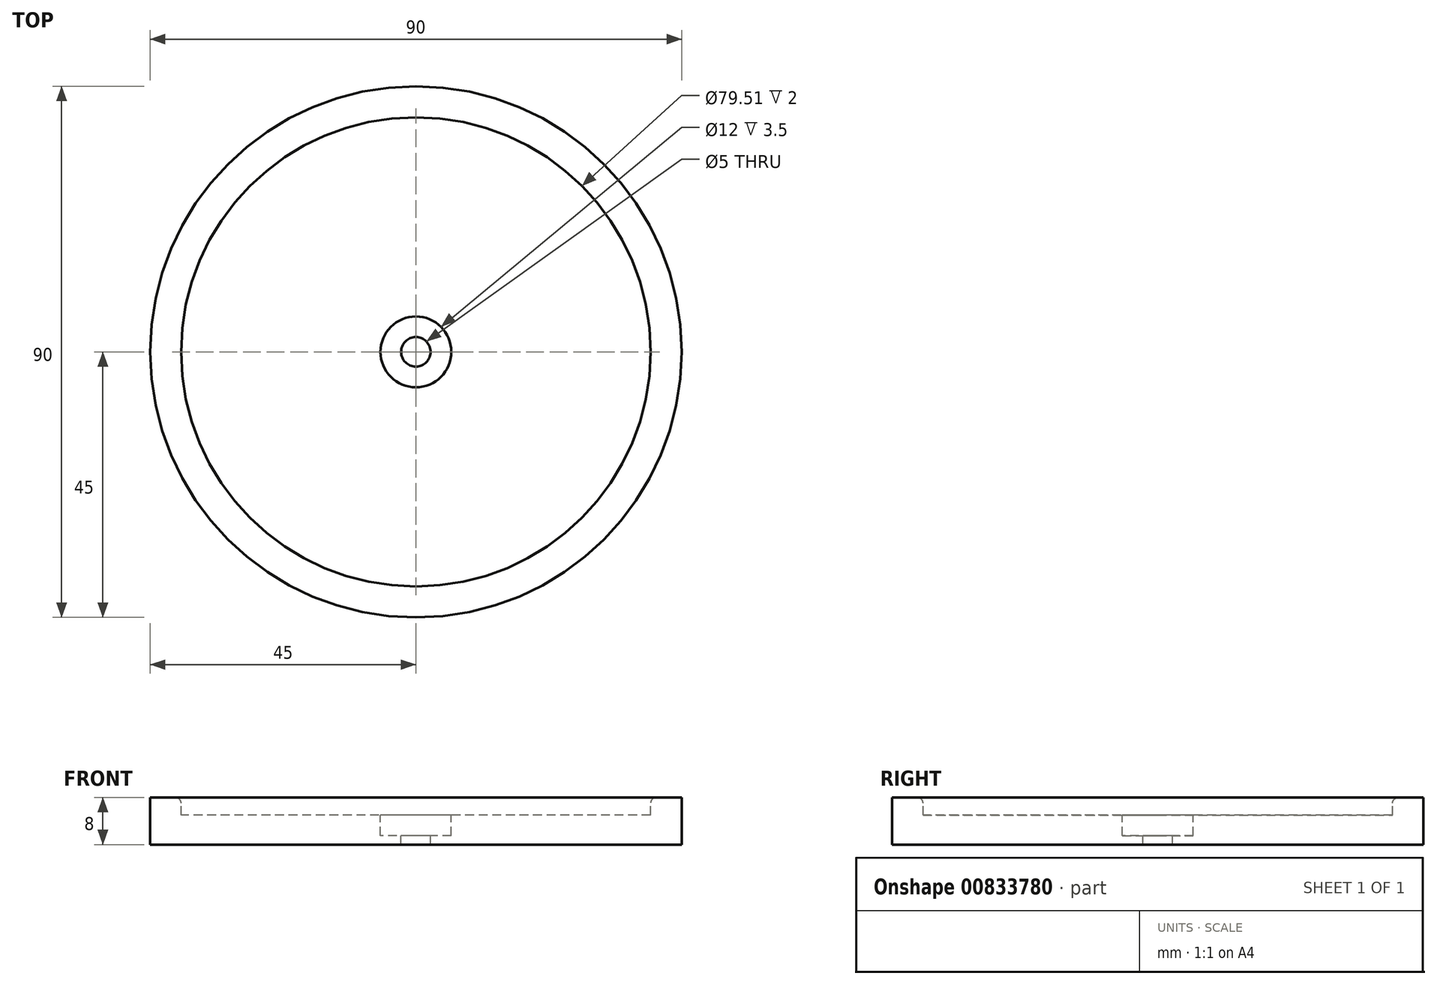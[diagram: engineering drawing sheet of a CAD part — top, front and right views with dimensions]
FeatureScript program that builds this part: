
annotation { "Feature Type Name" : "Feature", "Feature Type Description" : "" }
export const myFeature = defineFeature(function(context is Context, id is Id, definition is map)
    precondition{}
    {
        {
            var Q0;
            Q0=qCreatedBy(makeId("Front.planeOp"),FACE);
            var sketch = newSketch(context, id + "F0", { "sketchPlane" : qUnion([Q0])});
            skLineSegment(sketch, "E0", {"start": v(0, 45.14) * mm, "end": v(0, -36.73) * mm, "construction": true});
            skLineSegment(sketch, "E1.bottom", {"start": v(2.5, 0) * mm, "end": v(45, 0) * mm});
            skLineSegment(sketch, "E1.top", {"start": v(40.76, 8) * mm, "end": v(45, 8) * mm});
            skLineSegment(sketch, "E1.left", {"start": v(2.5, 0) * mm, "end": v(2.5, 1.5) * mm});
            skLineSegment(sketch, "E1.right", {"start": v(45, 0) * mm, "end": v(45, 8) * mm});
            skLineSegment(sketch, "E2", {"start": v(2.5, 1.5) * mm, "end": v(6, 1.5) * mm});
            skLineSegment(sketch, "E3", {"start": v(6, 1.5) * mm, "end": v(6, 5) * mm});
            skLineSegment(sketch, "E4", {"start": v(6, 5) * mm, "end": v(39.76, 5) * mm});
            skLineSegment(sketch, "E5", {"start": v(39.76, 5) * mm, "end": v(39.76, 7) * mm});
            skPoint(sketch, "E6.newPointA", {"position": v(39.76, 7.8) * mm});
            skPoint(sketch, "E6.newPointB", {"position": v(2.5, 8) * mm});
            skArc(sketch, "E6.filletArc", {"start": v(40.76, 8) * mm, "mid": v(40.05, 7.7) * mm, "end": v(39.76, 7) * mm});
            skSolve(sketch);
        }
        {
            var Q0;
            Q0 = qSketchRegion(id + "F0", true);
            var Q1;
            Q1=sQuery(id+"F0.wireOp",EDGE,"E0");
            revolve(context, id + "F1", {"surfaceOperationType" : NewSurfaceOperationType.NEW, "entities" : qUnion([Q0]), "axis" : qUnion([Q1]), "revolveType" : RevolveType.FULL});
        }
    });
